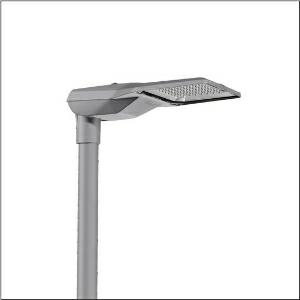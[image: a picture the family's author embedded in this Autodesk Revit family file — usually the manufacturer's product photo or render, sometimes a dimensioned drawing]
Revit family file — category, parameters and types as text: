
# Revit family: streetlight_sl_21_midi___stw1_0a_5xe3e43s08mb_fad8
name_source: partatom
category: Lighting Fixtures
units: mm (PartAtom-declared; Revit-internal decimal feet)

## family parameters
Cut with Voids When Loaded = No
Host = Face
Light Source = No
Part Type = Normal
Room Calculation Point = No
Round Connector Dimension = Use Diameter
Shared = No

## types (1)
- --- (1 x LED, 20180 lm, 147 W, 4000K)
    Apparent Load = 147 VA
    CIE Flux Codes = 38 75 98 100 100
    Color Rendering = 70
    Color Temperature = 4000K
    Default Elevation = 1800 mm
    Description = Streetlight SL 21 midi, mast luminaire, primary light control with lens, of PMMA, primary optical cover: cover, of toughened safety glass, transparent, light distribution: STW1.0a, light emission: direct distribution, primary light characteristic: asymmetric, installation type: side-entry, post-top, LED, High Power LED, rated luminous flux: 20.180lm, luminous efficacy: 137lm/W, light colour: 740, colour temperature: 4000K, control gear: D4i, control: overheat protection, constant luminous flux control, time-dependent luminous flux control, flexible luminous flux parameterisation, pre-setting: logarithmic dimming characteristic, mains connection: 230..240V, AC, 50/60Hz, start of lifetime: 147W, end of service life: 155W, reduction: 65W, luminaire housing, of diecast aluminium, powder-coated, Siteco® metallic grey (DB 702S), corrosivity category C5 mid according to DIN EN ISO 12944, please order mast flange separately, inclination adjustable: 0°, 5°, 10°, 15°, sealing non-destructively replaceable, multi-level sealing system, length: 644mm, width: 335mm, height: 110mm, mast flange for spigot size: 42mm (side-entry): 5XC10008XM4, 60/48mm (side-entry/post-top): 5XC10108XM2, 76/60mm (side-entry/post-top): 5XC10108XM1, mounting height: 4..8m, Smart Interface above, protection rating (complete): IP66, insulation class (complete): insulation class II (safety insulation), certification: CE, ENEC, ENEC+, VDE, impact resistance: IK10, permissible operating ambient temperature for outdoor applications: -40..+50°C, standard-compliant lighting for roads and squares, packaging unit: 1 piece

Light Distribution: STW1.0a
    Height = 111 mm
    Lamp = 1 x LED
    Lamp Light Flux = 20180 lm
    Lamp Power = 147 W
    Lamp count = 1
    Length = 644 mm
    Luminous efficacy = 137 lm/W
    Manufacturer = Siteco
    ModVariant = No
    Model = 5XE3E43S08MB
    Number of Poles = 1
    OnlyDefault = Yes
    Power Factor = 1
    Product Name = Streetlight SL 21 midi | STW1.0a
    Product group = mast luminaire | pylon top
    ProductGroupID = 6100
    Protection Class = Protection class II
    Protection Degree = IP 66
    RLX_Detail_Level = 1
    RLX_Emergency_Light_Flux = 0 lm
    RLX_Emergency_Type = 0
    RLX_Emergency_Type_DB = No
    RlxData = <blob elided: 26909 chars, md5=ce9a95ba>
    Socket = socket
    Standby Power = 0 W
    System Light Flux = 20180 lm
    System Power = 147 W
    Type Comments = factory setting: luminous flux: 100 % | dim-lin: 254 | 750 mA
    Type Image = l_1004302.jpg
    URL = http://relux.com
    VarID = @adj_187946
    Voltage = 0 V
    Weight = 0.00 kg
    Width = 336 mm

## geometry (parser evidence)
native form markers: Blend x4, Sweep x11
no freeform markers — native parametric forms only
